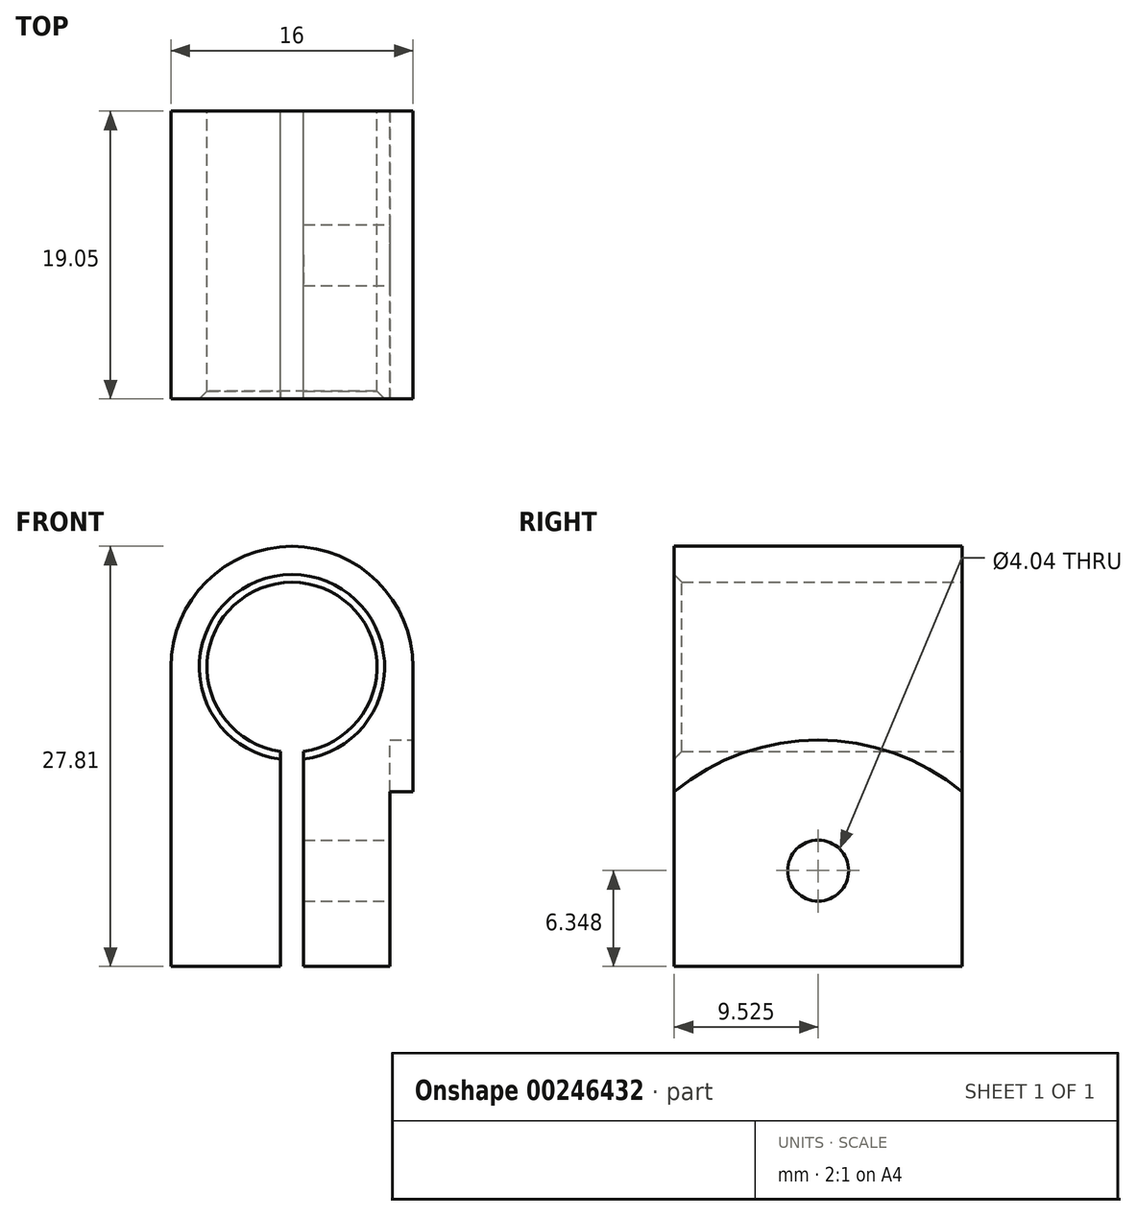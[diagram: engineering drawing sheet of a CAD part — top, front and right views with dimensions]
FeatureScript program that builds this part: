
annotation { "Feature Type Name" : "Feature", "Feature Type Description" : "" }
export const myFeature = defineFeature(function(context is Context, id is Id, definition is map)
    precondition{}
    {
        {
            var Q0;
            Q0=qCreatedBy(makeId("Front.planeOp"),FACE);
            var sketch = newSketch(context, id + "F0", { "sketchPlane" : qUnion([Q0])});
            skArc(sketch, "E0", {"start": v(8, 0) * mm, "mid": v(0, 8) * mm, "end": v(-8, 0) * mm});
            skLineSegment(sketch, "E1", {"start": v(-0.76, -19.81) * mm, "end": v(-0.76, -5.57) * mm});
            skLineSegment(sketch, "E2", {"start": v(-0.76, -19.81) * mm, "end": v(-8, -19.81) * mm});
            skLineSegment(sketch, "E3", {"start": v(-8, -19.81) * mm, "end": v(-8, 0) * mm});
            skLineSegment(sketch, "E4", {"start": v(0.76, -19.81) * mm, "end": v(8, -19.81) * mm});
            skLineSegment(sketch, "E5", {"start": v(8, -19.81) * mm, "end": v(8, 0) * mm});
            skLineSegment(sketch, "E6", {"start": v(0.76, -19.81) * mm, "end": v(0.76, -5.57) * mm});
            skArc(sketch, "E7", {"start": v(0.76, -5.57) * mm, "mid": v(0, 5.62) * mm, "end": v(-0.76, -5.57) * mm});
            skSolve(sketch);
        }
        {
            var Q0;
            Q0 = qSketchRegion(id + "F0", true);
            extrude(context, id + "F1", {"entities" : qUnion([Q0]), "depth" : 19.05 * mm});
        }
        {
            var Q0;
            Q0=makeQuery(id+"F1.opExtrude","CAP_EDGE",EDGE,{"disambiguationData":[OSD([sQuery(id+"F0.wireOp",EDGE,"E7")])],"isStart":false});
            chamfer(context, id + "F2", {"entities" : qUnion([Q0]), "width" : 0.5 * mm, "tangentPropagation" : true});
        }
        {
            var Q0;
            Q0=makeQuery(id+"F1.opExtrude","SWEPT_FACE",FACE,{"disambiguationData":[OSD([sQuery(id+"F0.wireOp",EDGE,"E5")])]});
            var sketch = newSketch(context, id + "F3", { "sketchPlane" : qUnion([Q0])});
            skArc(sketch, "E8", {"start": v(0, -8.24) * mm, "mid": v(-9.52, -4.83) * mm, "end": v(-19.05, -8.24) * mm});
            skLineSegment(sketch, "E9.0", {"start": v(-19.05, -19.81) * mm, "end": v(-19.05, -8.24) * mm});
            skLineSegment(sketch, "E9.1", {"start": v(-19.05, -19.81) * mm, "end": v(0, -19.81) * mm});
            skLineSegment(sketch, "E9.2", {"start": v(0, -19.81) * mm, "end": v(0, -8.24) * mm});
            skPoint(sketch, "E10.orphan", {"position": v(-19.05, 0) * mm});
            skPoint(sketch, "E11.orphan", {"position": v(0, 0) * mm});
            skSolve(sketch);
        }
        {
            var Q0;
            Q0 = qSketchRegion(id + "F3", true);
            extrude(context, id + "F4", {"entities" : qUnion([Q0]), "operationType" : NewBodyOperationType.REMOVE, "oppositeDirection" : true, "depth" : 1.52 * mm});
        }
        {
            var Q0;
            Q0=makeQuery(id+"F4.boolean.opBoolean","COPY",FACE,{"derivedFrom":makeQuery(id+"F4.opExtrude","CAP_FACE",FACE,{"disambiguationData":[OSD([sQuery(id+"F3.wireOp",EDGE,"E8"),sQuery(id+"F3.wireOp",EDGE,"E9.0"),sQuery(id+"F3.wireOp",EDGE,"E9.1"),sQuery(id+"F3.wireOp",EDGE,"E9.2")])],"isStart":false})});
            var sketch = newSketch(context, id + "F5", { "sketchPlane" : qUnion([Q0])});
            skPoint(sketch, "E12", {"position": v(-9.53, -13.46) * mm});
            skSolve(sketch);
        }
        {
            var Q0;
            Q0=sQuery(id+"F5.wireOp",VERTEX,"E12");
            var Q1;
            Q1=makeQuery(id+"F1.opExtrude","SWEPT_BODY",BODY,{"disambiguationData":[OSD([sQuery(id+"F0.wireOp",EDGE,"E0"),sQuery(id+"F0.wireOp",EDGE,"E1"),sQuery(id+"F0.wireOp",EDGE,"E2"),sQuery(id+"F0.wireOp",EDGE,"E3"),sQuery(id+"F0.wireOp",EDGE,"E4"),sQuery(id+"F0.wireOp",EDGE,"E5"),sQuery(id+"F0.wireOp",EDGE,"E6"),sQuery(id+"F0.wireOp",EDGE,"E7")])]});
            hole(context, id + "F6", {"style" : HoleStyle.SIMPLE, "endStyle" : HoleEndStyle.BLIND, "standardTappedOrClearance" : lookupTablePath({ "standard" : "ANSI", "engagement" : "75%", "pitch" : "32 tpi", "size" : "#10", "type" : "Tapped" }), "standardBlindInLast" : lookupTablePath({ "standard" : "ANSI", "engagement" : "75%", "pitch" : "32 tpi", "size" : "#10", "type" : "Tapped" }), "holeDiameter" : 4.04 * mm, "showTappedDepth" : true, "holeDepth" : 5.94 * mm, "tappedDepth" : 3.56 * mm, "tapClearance" : 3, "locations" : qUnion([Q0]), "scope" : qUnion([Q1]), "majorDiameter" : 4.83 * mm});
        }
    });
